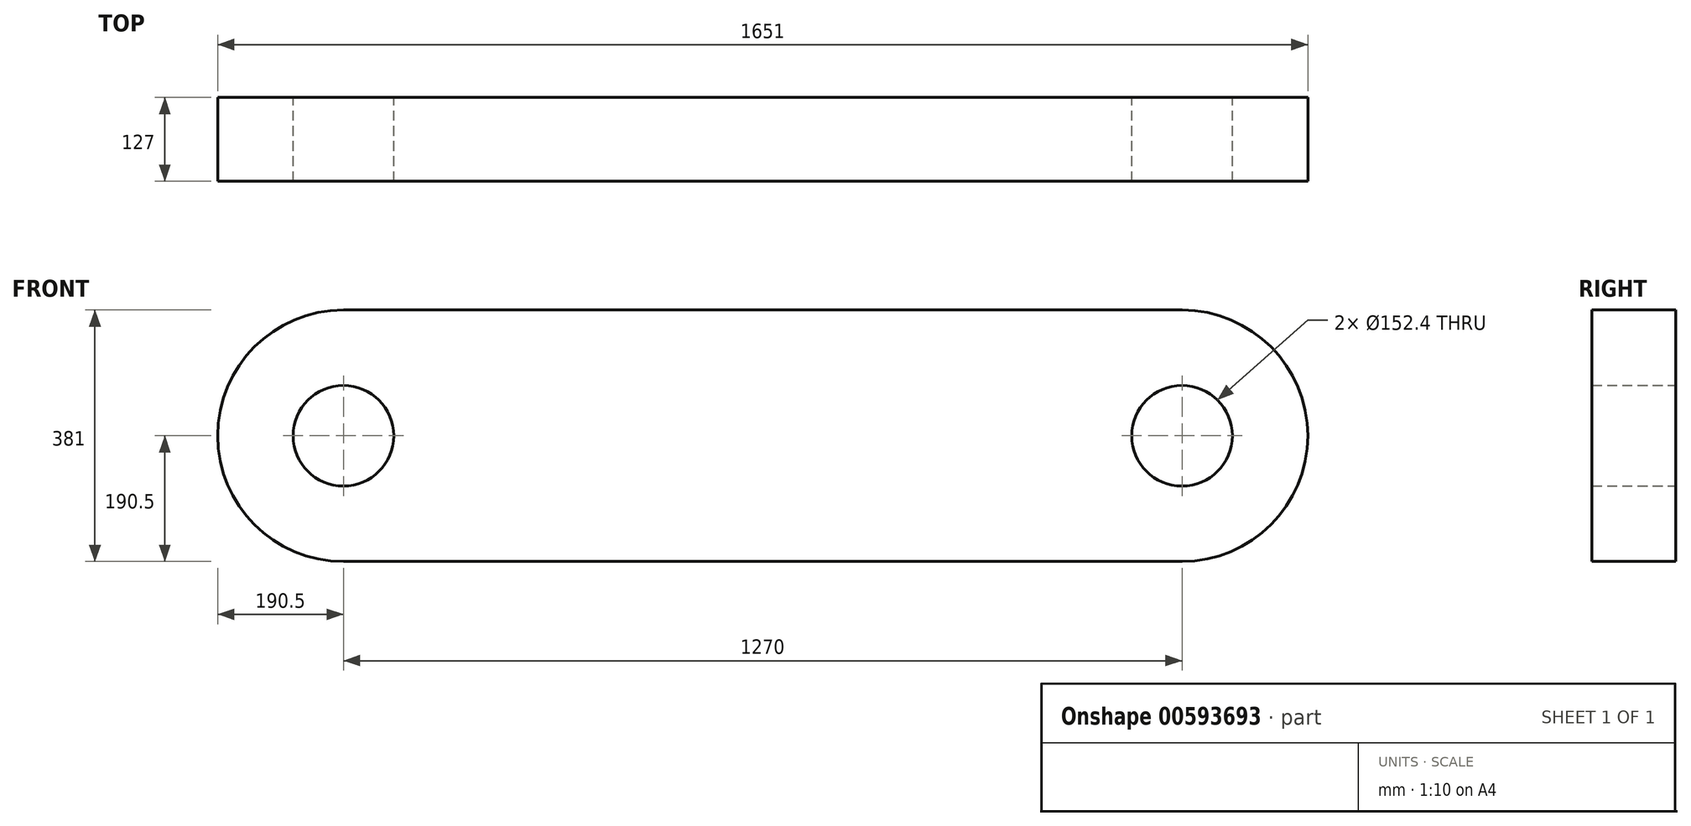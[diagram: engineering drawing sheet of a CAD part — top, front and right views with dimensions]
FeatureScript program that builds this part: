
annotation { "Feature Type Name" : "Feature", "Feature Type Description" : "" }
export const myFeature = defineFeature(function(context is Context, id is Id, definition is map)
    precondition{}
    {
        {
            var Q0;
            Q0=qCreatedBy(makeId("Front.planeOp"),FACE);
            var sketch = newSketch(context, id + "F0", { "sketchPlane" : qUnion([Q0])});
            skLineSegment(sketch, "E0.bottom", {"start": v(-635, 190.5) * mm, "end": v(635, 190.5) * mm});
            skLineSegment(sketch, "E0.top", {"start": v(-635, -190.5) * mm, "end": v(635, -190.5) * mm});
            skLineSegment(sketch, "E0.left", {"start": v(-635, 190.5) * mm, "end": v(-635, -190.5) * mm, "construction": true});
            skLineSegment(sketch, "E0.right", {"start": v(635, 190.5) * mm, "end": v(635, -190.5) * mm, "construction": true});
            skArc(sketch, "E1", {"start": v(-635, 190.5) * mm, "mid": v(-825.5, 0) * mm, "end": v(-635, -190.5) * mm});
            skArc(sketch, "E2.MirrorCS", {"start": v(635, 190.5) * mm, "mid": v(825.5, 0) * mm, "end": v(635, -190.5) * mm});
            skCircle(sketch, "E3", {"center": v(-635, 0) * mm, "radius": 76.2 * mm});
            skCircle(sketch, "E4", {"center": v(635, 0) * mm, "radius": 76.2 * mm});
            skSolve(sketch);
        }
        {
            var Q0;
            Q0 = qSketchRegion(id + "F0", true);
            extrude(context, id + "F1", {"entities" : qUnion([Q0]), "depth" : 127 * mm, "offsetDistance" : 25.4 * mm});
        }
    });
